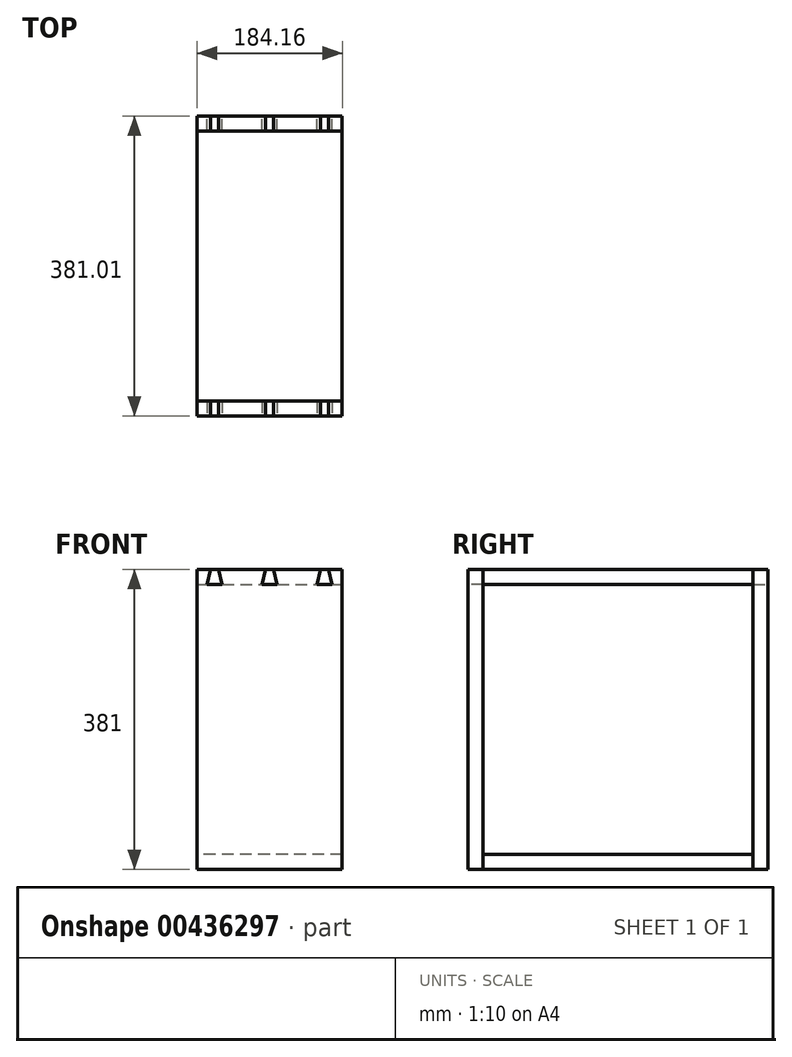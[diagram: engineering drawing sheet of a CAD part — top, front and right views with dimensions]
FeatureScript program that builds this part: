
annotation { "Feature Type Name" : "Feature", "Feature Type Description" : "" }
export const myFeature = defineFeature(function(context is Context, id is Id, definition is map)
    precondition{}
    {
        {
            var Q0;
            Q0=qCreatedBy(makeId("Front.planeOp"),FACE);
            var sketch = newSketch(context, id + "F0", { "sketchPlane" : qUnion([Q0])});
            skLineSegment(sketch, "E0.bottom", {"start": v(-92.08, 190.5) * mm, "end": v(92.08, 190.5) * mm});
            skLineSegment(sketch, "E0.top", {"start": v(-92.08, -190.5) * mm, "end": v(92.08, -190.5) * mm});
            skLineSegment(sketch, "E0.left", {"start": v(-92.08, 190.5) * mm, "end": v(-92.08, -190.5) * mm});
            skLineSegment(sketch, "E0.right", {"start": v(92.08, 190.5) * mm, "end": v(92.08, -190.5) * mm});
            skLineSegment(sketch, "E1", {"start": v(0, 190.5) * mm, "end": v(0, -190.5) * mm, "construction": true});
            skLineSegment(sketch, "E2", {"start": v(92.08, 0) * mm, "end": v(-92.08, 0) * mm, "construction": true});
            skLineSegment(sketch, "E3", {"start": v(-74.93, 190.5) * mm, "end": v(-79.38, 171.45) * mm});
            skLineSegment(sketch, "E4", {"start": v(-79.38, 171.45) * mm, "end": v(-60.33, 171.45) * mm});
            skLineSegment(sketch, "E5", {"start": v(-60.33, 171.45) * mm, "end": v(-64.77, 190.5) * mm});
            skLineSegment(sketch, "E6.1.0.0", {"start": v(-9.53, 171.45) * mm, "end": v(9.52, 171.45) * mm});
            skLineSegment(sketch, "E6.1.0.1", {"start": v(-5.08, 190.5) * mm, "end": v(-9.52, 171.45) * mm});
            skLineSegment(sketch, "E6.1.0.2", {"start": v(9.52, 171.45) * mm, "end": v(5.08, 190.5) * mm});
            skLineSegment(sketch, "E6.2.0.0", {"start": v(60.33, 171.45) * mm, "end": v(79.37, 171.45) * mm});
            skLineSegment(sketch, "E6.2.0.1", {"start": v(64.77, 190.5) * mm, "end": v(60.33, 171.45) * mm});
            skLineSegment(sketch, "E6.2.0.2", {"start": v(79.37, 171.45) * mm, "end": v(74.93, 190.5) * mm});
            skLineSegment(sketch, "E6.direction1", {"start": v(-79.38, 171.45) * mm, "end": v(-9.53, 171.45) * mm, "construction": true});
            skSolve(sketch);
        }
        {
            var Q0;
            Q0=makeQuery(id+"F0.imprint","IMPRINT",FACE,{"disambiguationData":[TD([[makeQuery(id+"F0.imprint","IMPRINT",EDGE,{"derivedFrom":sQuery(id+"F0.wireOp",EDGE,"E0.top")}),1.0]])]});
            var Q1;
            {var subQ0=sQuery(id+"F0.wireOp",EDGE,"E3");Q1=makeQuery(id+"F0.imprint","IMPRINT",FACE,{"disambiguationData":[TD([[makeQuery(id+"F0.imprint","IMPRINT",EDGE,{"derivedFrom":subQ0}),1.0]])]});}
            var Q2;
            Q2=makeQuery(id+"F0.imprint","IMPRINT",FACE,{"disambiguationData":[TD([[makeQuery(id+"F0.imprint","IMPRINT",EDGE,{"derivedFrom":sQuery(id+"F0.wireOp",EDGE,"E6.1.0.0")}),1.0]])]});
            var Q3;
            Q3=makeQuery(id+"F0.imprint","IMPRINT",FACE,{"disambiguationData":[TD([[makeQuery(id+"F0.imprint","IMPRINT",EDGE,{"derivedFrom":sQuery(id+"F0.wireOp",EDGE,"E6.2.0.0")}),1.0]])]});
            extrude(context, id + "F1", {"entities" : qUnion([Q0, Q1, Q2, Q3]), "endBound" : BoundingType.SYMMETRIC, "depth" : 19.05 * mm});
        }
        {
            var Q0;
            {var subQ0=sQuery(id+"F0.wireOp",EDGE,"E3");Q0=makeQuery(id+"F0.imprint","IMPRINT",FACE,{"disambiguationData":[TD([[makeQuery(id+"F0.imprint","IMPRINT",EDGE,{"derivedFrom":subQ0}),1.0]])]});}
            var Q1;
            Q1=makeQuery(id+"F0.imprint","IMPRINT",FACE,{"disambiguationData":[TD([[makeQuery(id+"F0.imprint","IMPRINT",EDGE,{"derivedFrom":sQuery(id+"F0.wireOp",EDGE,"E6.1.0.0")}),1.0]])]});
            var Q2;
            Q2=makeQuery(id+"F0.imprint","IMPRINT",FACE,{"disambiguationData":[TD([[makeQuery(id+"F0.imprint","IMPRINT",EDGE,{"derivedFrom":sQuery(id+"F0.wireOp",EDGE,"E6.2.0.0")}),1.0]])]});
            extrude(context, id + "F2", {"entities" : qUnion([Q0, Q1, Q2]), "operationType" : NewBodyOperationType.REMOVE, "endBound" : BoundingType.SYMMETRIC, "oppositeDirection" : true, "depth" : 19.05 * mm});
        }
        {
            var Q0;
            Q0=makeQuery(id+"F1.opExtrude","CAP_FACE",FACE,{"disambiguationData":[OSD([sQuery(id+"F0.wireOp",EDGE,"E0.bottom"),sQuery(id+"F0.wireOp",EDGE,"E0.top"),sQuery(id+"F0.wireOp",EDGE,"E0.left"),sQuery(id+"F0.wireOp",EDGE,"E0.right")])],"isStart":true});
            var sketch = newSketch(context, id + "F3", { "sketchPlane" : qUnion([Q0])});
            skLineSegment(sketch, "E7.bottom", {"start": v(-92.07, -190.5) * mm, "end": v(92.08, -190.5) * mm});
            skLineSegment(sketch, "E7.top", {"start": v(-92.08, -171.45) * mm, "end": v(92.07, -171.45) * mm});
            skLineSegment(sketch, "E7.left", {"start": v(-92.07, -190.5) * mm, "end": v(-92.07, -171.45) * mm});
            skLineSegment(sketch, "E7.right", {"start": v(92.08, -190.5) * mm, "end": v(92.08, -171.45) * mm});
            skSolve(sketch);
        }
        {
            var Q0;
            Q0 = qSketchRegion(id + "F3", true);
            extrude(context, id + "F4", {"entities" : qUnion([Q0]), "depth" : 361.95 * mm, "hasSecondDirection" : true, "secondDirectionOppositeDirection" : true, "secondDirectionDepth" : 19.05 * mm});
        }
        {
            var Q0;
            Q0=makeQuery(id+"F1.opExtrude","SWEPT_BODY",BODY,{"disambiguationData":[OSD([sQuery(id+"F0.wireOp",EDGE,"E0.bottom"),sQuery(id+"F0.wireOp",EDGE,"E0.top"),sQuery(id+"F0.wireOp",EDGE,"E0.left"),sQuery(id+"F0.wireOp",EDGE,"E0.right")])]});
            var Q1;
            Q1=makeQuery(id+"F4.opExtrude","SWEPT_BODY",BODY,{"disambiguationData":[OSD([sQuery(id+"F3.wireOp",EDGE,"E7.bottom"),sQuery(id+"F3.wireOp",EDGE,"E7.top"),sQuery(id+"F3.wireOp",EDGE,"E7.left"),sQuery(id+"F3.wireOp",EDGE,"E7.right")])]});
            booleanBodies(context, id + "F5", {"operationType" : BooleanOperationType.SUBTRACTION, "tools" : qUnion([Q0]), "targets" : qUnion([Q1]), "keepTools" : true});
        }
        {
            var Q0;
            Q0=makeQuery(id+"F1.opExtrude","CAP_FACE",FACE,{"disambiguationData":[OSD([sQuery(id+"F0.wireOp",EDGE,"E0.bottom"),sQuery(id+"F0.wireOp",EDGE,"E0.top"),sQuery(id+"F0.wireOp",EDGE,"E0.left"),sQuery(id+"F0.wireOp",EDGE,"E0.right")])],"isStart":false});
            cPlane(context, id + "F6", {"entities" : qUnion([Q0]), "cplaneType" : CPlaneType.OFFSET, "offset" : 190.5 * mm, "oppositeDirection" : true, "width" : 152.4 * mm, "height" : 152.4 * mm});
        }
        {
            var Q0;
            Q0=makeQuery(id+"F1.opExtrude","SWEPT_BODY",BODY,{"disambiguationData":[OSD([sQuery(id+"F0.wireOp",EDGE,"E0.bottom"),sQuery(id+"F0.wireOp",EDGE,"E0.top"),sQuery(id+"F0.wireOp",EDGE,"E0.left"),sQuery(id+"F0.wireOp",EDGE,"E0.right")])]});
            var Q1;
            Q1=qCreatedBy(id+"F6.planeOp",FACE);
            mirror(context, id + "F7", {"entities" : qUnion([Q0]), "mirrorPlane" : qUnion([Q1])});
        }
        {
            var Q0;
            Q0=makeQuery(id+"F7.opPattern","COPY",BODY,{"derivedFrom":makeQuery(id+"F1.opExtrude","SWEPT_BODY",BODY,{"disambiguationData":[OSD([sQuery(id+"F0.wireOp",EDGE,"E0.bottom"),sQuery(id+"F0.wireOp",EDGE,"E0.top"),sQuery(id+"F0.wireOp",EDGE,"E0.left"),sQuery(id+"F0.wireOp",EDGE,"E0.right")])]}),"instanceName":"1"});
            var Q1;
            Q1=makeQuery(id+"F4.opExtrude","SWEPT_BODY",BODY,{"disambiguationData":[OSD([sQuery(id+"F3.wireOp",EDGE,"E7.bottom"),sQuery(id+"F3.wireOp",EDGE,"E7.top"),sQuery(id+"F3.wireOp",EDGE,"E7.left"),sQuery(id+"F3.wireOp",EDGE,"E7.right")])]});
            booleanBodies(context, id + "F8", {"operationType" : BooleanOperationType.SUBTRACTION, "tools" : qUnion([Q0]), "targets" : qUnion([Q1]), "keepTools" : true});
        }
        {
            var Q0;
            Q0=makeQuery(id+"F4.opExtrude","SWEPT_BODY",BODY,{"disambiguationData":[OSD([sQuery(id+"F3.wireOp",EDGE,"E7.bottom"),sQuery(id+"F3.wireOp",EDGE,"E7.top"),sQuery(id+"F3.wireOp",EDGE,"E7.left"),sQuery(id+"F3.wireOp",EDGE,"E7.right")])]});
            var Q1;
            Q1=qCreatedBy(makeId("Top.planeOp"),FACE);
            mirror(context, id + "F9", {"entities" : qUnion([Q0]), "mirrorPlane" : qUnion([Q1])});
        }
    });
